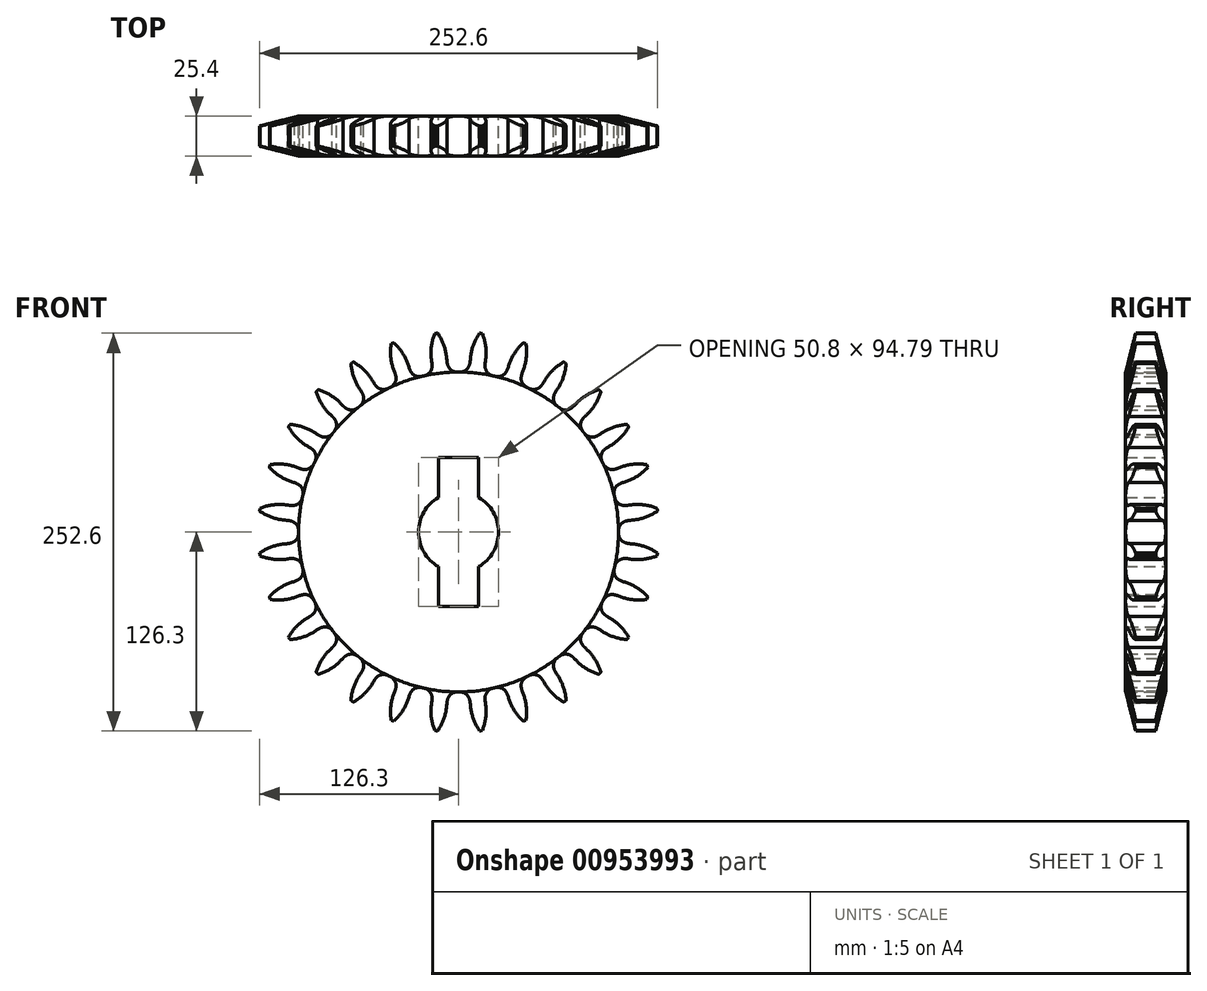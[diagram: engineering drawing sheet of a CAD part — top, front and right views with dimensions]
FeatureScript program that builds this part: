
annotation { "Feature Type Name" : "Feature", "Feature Type Description" : "" }
export const myFeature = defineFeature(function(context is Context, id is Id, definition is map)
    precondition{}
    {
        {
            var Q0;
            Q0=qCreatedBy(makeId("Front.planeOp"),FACE);
            var sketch = newSketch(context, id + "F0", { "sketchPlane" : qUnion([Q0])});
            skCircle(sketch, "E0", {"center": v(0, 0) * mm, "radius": 127 * mm});
            skLineSegment(sketch, "E1", {"start": v(0, 0) * mm, "end": v(0, 164.21) * mm, "construction": true});
            skLineSegment(sketch, "E2", {"start": v(0, 0) * mm, "end": v(174.47, 0) * mm, "construction": true});
            skCircle(sketch, "E3", {"center": v(0, 0) * mm, "radius": 25.4 * mm});
            skLineSegment(sketch, "E4.bottom", {"start": v(12.7, 47.4) * mm, "end": v(-12.7, 47.4) * mm});
            skLineSegment(sketch, "E4.top", {"start": v(12.7, -47.4) * mm, "end": v(-12.7, -47.4) * mm});
            skLineSegment(sketch, "E4.left", {"start": v(12.7, 47.4) * mm, "end": v(12.7, 22) * mm});
            skLineSegment(sketch, "E4.right", {"start": v(-12.7, 47.4) * mm, "end": v(-12.7, 22) * mm});
            skLineSegment(sketch, "E5.trimOffspring", {"start": v(-12.7, -22) * mm, "end": v(-12.7, -47.4) * mm});
            skLineSegment(sketch, "E6.trimOffspring", {"start": v(12.7, -22) * mm, "end": v(12.7, -47.4) * mm});
            skSolve(sketch);
        }
        {
            var Q0;
            Q0=makeQuery(id+"F0.imprint","IMPRINT",FACE,{"disambiguationData":[TD([[makeQuery(id+"F0.imprint","IMPRINT",EDGE,{"derivedFrom":sQuery(id+"F0.wireOp",EDGE,"E0")}),1.0]])]});
            extrude(context, id + "F1", {"entities" : qUnion([Q0]), "depth" : 25.4 * mm, "offsetDistance" : 25.4 * mm});
        }
        {
            var Q0;
            Q0=makeQuery(id+"F1.opExtrude","CAP_EDGE",EDGE,{"disambiguationData":[OSD([sQuery(id+"F0.wireOp",EDGE,"E0")])],"isStart":false});
            var Q1;
            Q1=makeQuery(id+"F1.opExtrude","CAP_EDGE",EDGE,{"disambiguationData":[OSD([sQuery(id+"F0.wireOp",EDGE,"E0")])],"isStart":true});
            chamfer(context, id + "F2", {"entities" : qUnion([Q0, Q1]), "chamferType" : ChamferType.TWO_OFFSETS, "width1" : 25.4 * mm, "oppositeDirection" : false, "width2" : 6.35 * mm, "tangentPropagation" : true});
        }
        {
            var Q0;
            Q0=makeQuery(id+"F0.imprint","IMPRINT",FACE,{"disambiguationData":[TD([[makeQuery(id+"F0.imprint","IMPRINT",EDGE,{"derivedFrom":sQuery(id+"F0.wireOp",EDGE,"E0")}),1.0]])]});
            var sketch = newSketch(context, id + "F3", { "sketchPlane" : qUnion([Q0])});
            skArc(sketch, "E7", {"start": v(0.8, 101.6) * mm, "mid": v(0, 101.6) * mm, "end": v(-0.8, 101.6) * mm});
            skLineSegment(sketch, "E8", {"start": v(-7.41, 108.46) * mm, "end": v(-7.1, 106.78) * mm});
            skLineSegment(sketch, "E9.MirrorCS", {"start": v(7.41, 108.46) * mm, "end": v(7.1, 106.78) * mm});
            skPoint(sketch, "E10.endSnap0", {"position": v(0, 101.6) * mm});
            skPoint(sketch, "E11.visualSharp", {"position": v(-6.1, 101.42) * mm});
            skArc(sketch, "E11.filletArc", {"start": v(-7.1, 106.78) * mm, "mid": v(-4.9, 103.04) * mm, "end": v(-0.8, 101.6) * mm});
            skPoint(sketch, "E12.visualSharp", {"position": v(6.1, 101.42) * mm});
            skArc(sketch, "E12.filletArc", {"start": v(0.8, 101.6) * mm, "mid": v(4.9, 103.04) * mm, "end": v(7.1, 106.78) * mm});
            skArc(sketch, "E13", {"start": v(22.64, 135.32) * mm, "mid": v(11.73, 123.75) * mm, "end": v(7.41, 108.46) * mm});
            skArc(sketch, "E14.MirrorCS", {"start": v(-22.64, 135.32) * mm, "mid": v(-11.73, 123.75) * mm, "end": v(-7.41, 108.46) * mm});
            skArc(sketch, "E15.1.0", {"start": v(-8.04, 136.96) * mm, "mid": v(-16.1, 123.26) * mm, "end": v(-16.9, 107.39) * mm});
            skArc(sketch, "E15.1.1", {"start": v(-52.18, 126.89) * mm, "mid": v(-38.98, 118.04) * mm, "end": v(-31.36, 104.09) * mm});
            skPoint(sketch, "E15.1.2", {"position": v(-16.63, 100.23) * mm});
            skPoint(sketch, "E15.1.3", {"position": v(-28.5, 97.52) * mm});
            skPoint(sketch, "E15.1.4", {"position": v(-22.6, 99.05) * mm});
            skArc(sketch, "E15.1.5", {"start": v(-30.68, 102.52) * mm, "mid": v(-27.7, 99.37) * mm, "end": v(-23.4, 98.87) * mm});
            skLineSegment(sketch, "E15.1.6", {"start": v(-31.36, 104.09) * mm, "end": v(-30.68, 102.52) * mm});
            skArc(sketch, "E15.1.7", {"start": v(-21.82, 99.23) * mm, "mid": v(-18.16, 101.55) * mm, "end": v(-16.84, 105.68) * mm});
            skLineSegment(sketch, "E15.1.8", {"start": v(-16.9, 107.39) * mm, "end": v(-16.84, 105.68) * mm});
            skArc(sketch, "E15.1.9", {"start": v(-21.82, 99.23) * mm, "mid": v(-22.6, 99.05) * mm, "end": v(-23.4, 98.87) * mm});
            skArc(sketch, "E15.2.0", {"start": v(-38.32, 131.74) * mm, "mid": v(-43.12, 116.59) * mm, "end": v(-40.38, 100.93) * mm});
            skArc(sketch, "E15.2.1", {"start": v(-79.1, 112.1) * mm, "mid": v(-64.27, 106.4) * mm, "end": v(-53.74, 94.5) * mm});
            skPoint(sketch, "E15.2.2", {"position": v(-38.51, 94.02) * mm});
            skPoint(sketch, "E15.2.3", {"position": v(-49.5, 88.73) * mm});
            skPoint(sketch, "E15.2.4", {"position": v(-44.08, 91.54) * mm});
            skArc(sketch, "E15.2.5", {"start": v(-52.72, 93.12) * mm, "mid": v(-49.12, 90.72) * mm, "end": v(-44.8, 91.19) * mm});
            skLineSegment(sketch, "E15.2.6", {"start": v(-53.74, 94.5) * mm, "end": v(-52.72, 93.12) * mm});
            skArc(sketch, "E15.2.7", {"start": v(-43.35, 91.89) * mm, "mid": v(-40.3, 94.96) * mm, "end": v(-39.93, 99.28) * mm});
            skLineSegment(sketch, "E15.2.8", {"start": v(-40.38, 100.93) * mm, "end": v(-39.93, 99.28) * mm});
            skArc(sketch, "E15.2.9", {"start": v(-43.35, 91.89) * mm, "mid": v(-44.08, 91.54) * mm, "end": v(-44.8, 91.19) * mm});
            skArc(sketch, "E15.3.0", {"start": v(-66.67, 119.91) * mm, "mid": v(-67.98, 104.07) * mm, "end": v(-61.83, 89.42) * mm});
            skArc(sketch, "E15.3.1", {"start": v(-102.07, 91.68) * mm, "mid": v(-86.33, 89.44) * mm, "end": v(-73.42, 80.17) * mm});
            skPoint(sketch, "E15.3.2", {"position": v(-58.47, 83.1) * mm});
            skPoint(sketch, "E15.3.3", {"position": v(-68, 75.5) * mm});
            skPoint(sketch, "E15.3.4", {"position": v(-63.35, 79.43) * mm});
            skArc(sketch, "E15.3.5", {"start": v(-72.12, 79.05) * mm, "mid": v(-68.07, 77.51) * mm, "end": v(-63.98, 78.93) * mm});
            skLineSegment(sketch, "E15.3.6", {"start": v(-73.42, 80.17) * mm, "end": v(-72.12, 79.05) * mm});
            skArc(sketch, "E15.3.7", {"start": v(-62.71, 79.93) * mm, "mid": v(-60.42, 83.61) * mm, "end": v(-61.02, 87.9) * mm});
            skLineSegment(sketch, "E15.3.8", {"start": v(-61.83, 89.42) * mm, "end": v(-61.02, 87.9) * mm});
            skArc(sketch, "E15.3.9", {"start": v(-62.71, 79.93) * mm, "mid": v(-63.35, 79.43) * mm, "end": v(-63.98, 78.93) * mm});
            skArc(sketch, "E15.4.0", {"start": v(-91.68, 102.07) * mm, "mid": v(-89.44, 86.33) * mm, "end": v(-80.17, 73.42) * mm});
            skArc(sketch, "E15.4.1", {"start": v(-119.91, 66.67) * mm, "mid": v(-104.07, 67.98) * mm, "end": v(-89.42, 61.83) * mm});
            skPoint(sketch, "E15.4.2", {"position": v(-75.5, 68) * mm});
            skPoint(sketch, "E15.4.3", {"position": v(-83.1, 58.47) * mm});
            skPoint(sketch, "E15.4.4", {"position": v(-79.43, 63.35) * mm});
            skArc(sketch, "E15.4.5", {"start": v(-87.9, 61.02) * mm, "mid": v(-83.61, 60.42) * mm, "end": v(-79.93, 62.71) * mm});
            skLineSegment(sketch, "E15.4.6", {"start": v(-89.42, 61.83) * mm, "end": v(-87.9, 61.02) * mm});
            skArc(sketch, "E15.4.7", {"start": v(-78.93, 63.98) * mm, "mid": v(-77.51, 68.07) * mm, "end": v(-79.05, 72.12) * mm});
            skLineSegment(sketch, "E15.4.8", {"start": v(-80.17, 73.42) * mm, "end": v(-79.05, 72.12) * mm});
            skArc(sketch, "E15.4.9", {"start": v(-78.93, 63.98) * mm, "mid": v(-79.43, 63.35) * mm, "end": v(-79.93, 62.71) * mm});
            skArc(sketch, "E15.5.0", {"start": v(-112.1, 79.1) * mm, "mid": v(-106.4, 64.27) * mm, "end": v(-94.5, 53.74) * mm});
            skArc(sketch, "E15.5.1", {"start": v(-131.74, 38.32) * mm, "mid": v(-116.59, 43.12) * mm, "end": v(-100.93, 40.38) * mm});
            skPoint(sketch, "E15.5.2", {"position": v(-88.73, 49.5) * mm});
            skPoint(sketch, "E15.5.3", {"position": v(-94.02, 38.51) * mm});
            skPoint(sketch, "E15.5.4", {"position": v(-91.54, 44.08) * mm});
            skArc(sketch, "E15.5.5", {"start": v(-99.28, 39.93) * mm, "mid": v(-94.96, 40.3) * mm, "end": v(-91.89, 43.35) * mm});
            skLineSegment(sketch, "E15.5.6", {"start": v(-100.93, 40.38) * mm, "end": v(-99.28, 39.93) * mm});
            skArc(sketch, "E15.5.7", {"start": v(-91.19, 44.8) * mm, "mid": v(-90.72, 49.12) * mm, "end": v(-93.12, 52.72) * mm});
            skLineSegment(sketch, "E15.5.8", {"start": v(-94.5, 53.74) * mm, "end": v(-93.12, 52.72) * mm});
            skArc(sketch, "E15.5.9", {"start": v(-91.19, 44.8) * mm, "mid": v(-91.54, 44.08) * mm, "end": v(-91.89, 43.35) * mm});
            skArc(sketch, "E15.6.0", {"start": v(-126.89, 52.18) * mm, "mid": v(-118.04, 38.98) * mm, "end": v(-104.09, 31.36) * mm});
            skArc(sketch, "E15.6.1", {"start": v(-136.96, 8.04) * mm, "mid": v(-123.26, 16.1) * mm, "end": v(-107.39, 16.9) * mm});
            skPoint(sketch, "E15.6.2", {"position": v(-97.52, 28.5) * mm});
            skPoint(sketch, "E15.6.3", {"position": v(-100.23, 16.63) * mm});
            skPoint(sketch, "E15.6.4", {"position": v(-99.05, 22.6) * mm});
            skArc(sketch, "E15.6.5", {"start": v(-105.68, 16.84) * mm, "mid": v(-101.55, 18.16) * mm, "end": v(-99.23, 21.82) * mm});
            skLineSegment(sketch, "E15.6.6", {"start": v(-107.39, 16.9) * mm, "end": v(-105.68, 16.84) * mm});
            skArc(sketch, "E15.6.7", {"start": v(-98.87, 23.4) * mm, "mid": v(-99.37, 27.7) * mm, "end": v(-102.52, 30.68) * mm});
            skLineSegment(sketch, "E15.6.8", {"start": v(-104.09, 31.36) * mm, "end": v(-102.52, 30.68) * mm});
            skArc(sketch, "E15.6.9", {"start": v(-98.87, 23.4) * mm, "mid": v(-99.05, 22.6) * mm, "end": v(-99.23, 21.82) * mm});
            skArc(sketch, "E15.7.0", {"start": v(-135.32, 22.64) * mm, "mid": v(-123.75, 11.73) * mm, "end": v(-108.46, 7.41) * mm});
            skArc(sketch, "E15.7.1", {"start": v(-135.32, -22.64) * mm, "mid": v(-123.75, -11.73) * mm, "end": v(-108.46, -7.41) * mm});
            skPoint(sketch, "E15.7.2", {"position": v(-101.42, 6.1) * mm});
            skPoint(sketch, "E15.7.3", {"position": v(-101.42, -6.1) * mm});
            skPoint(sketch, "E15.7.4", {"position": v(-101.6, 0) * mm});
            skArc(sketch, "E15.7.5", {"start": v(-106.78, -7.1) * mm, "mid": v(-103.04, -4.9) * mm, "end": v(-101.6, -0.8) * mm});
            skLineSegment(sketch, "E15.7.6", {"start": v(-108.46, -7.41) * mm, "end": v(-106.78, -7.1) * mm});
            skArc(sketch, "E15.7.7", {"start": v(-101.6, 0.8) * mm, "mid": v(-103.04, 4.9) * mm, "end": v(-106.78, 7.1) * mm});
            skLineSegment(sketch, "E15.7.8", {"start": v(-108.46, 7.41) * mm, "end": v(-106.78, 7.1) * mm});
            skArc(sketch, "E15.7.9", {"start": v(-101.6, 0.8) * mm, "mid": v(-101.6, 0) * mm, "end": v(-101.6, -0.8) * mm});
            skArc(sketch, "E15.8.0", {"start": v(-136.96, -8.04) * mm, "mid": v(-123.26, -16.1) * mm, "end": v(-107.39, -16.9) * mm});
            skArc(sketch, "E15.8.1", {"start": v(-126.89, -52.18) * mm, "mid": v(-118.04, -38.98) * mm, "end": v(-104.09, -31.36) * mm});
            skPoint(sketch, "E15.8.2", {"position": v(-100.23, -16.63) * mm});
            skPoint(sketch, "E15.8.3", {"position": v(-97.52, -28.5) * mm});
            skPoint(sketch, "E15.8.4", {"position": v(-99.05, -22.6) * mm});
            skArc(sketch, "E15.8.5", {"start": v(-102.52, -30.68) * mm, "mid": v(-99.37, -27.7) * mm, "end": v(-98.87, -23.4) * mm});
            skLineSegment(sketch, "E15.8.6", {"start": v(-104.09, -31.36) * mm, "end": v(-102.52, -30.68) * mm});
            skArc(sketch, "E15.8.7", {"start": v(-99.23, -21.82) * mm, "mid": v(-101.55, -18.16) * mm, "end": v(-105.68, -16.84) * mm});
            skLineSegment(sketch, "E15.8.8", {"start": v(-107.39, -16.9) * mm, "end": v(-105.68, -16.84) * mm});
            skArc(sketch, "E15.8.9", {"start": v(-99.23, -21.82) * mm, "mid": v(-99.05, -22.6) * mm, "end": v(-98.87, -23.4) * mm});
            skArc(sketch, "E15.9.0", {"start": v(-131.74, -38.32) * mm, "mid": v(-116.59, -43.12) * mm, "end": v(-100.93, -40.38) * mm});
            skArc(sketch, "E15.9.1", {"start": v(-112.1, -79.1) * mm, "mid": v(-106.4, -64.27) * mm, "end": v(-94.5, -53.74) * mm});
            skPoint(sketch, "E15.9.2", {"position": v(-94.02, -38.51) * mm});
            skPoint(sketch, "E15.9.3", {"position": v(-88.73, -49.5) * mm});
            skPoint(sketch, "E15.9.4", {"position": v(-91.54, -44.08) * mm});
            skArc(sketch, "E15.9.5", {"start": v(-93.12, -52.72) * mm, "mid": v(-90.72, -49.12) * mm, "end": v(-91.19, -44.8) * mm});
            skLineSegment(sketch, "E15.9.6", {"start": v(-94.5, -53.74) * mm, "end": v(-93.12, -52.72) * mm});
            skArc(sketch, "E15.9.7", {"start": v(-91.89, -43.35) * mm, "mid": v(-94.96, -40.3) * mm, "end": v(-99.28, -39.93) * mm});
            skLineSegment(sketch, "E15.9.8", {"start": v(-100.93, -40.38) * mm, "end": v(-99.28, -39.93) * mm});
            skArc(sketch, "E15.9.9", {"start": v(-91.89, -43.35) * mm, "mid": v(-91.54, -44.08) * mm, "end": v(-91.19, -44.8) * mm});
            skArc(sketch, "E15.10.0", {"start": v(-119.91, -66.67) * mm, "mid": v(-104.07, -67.98) * mm, "end": v(-89.42, -61.83) * mm});
            skArc(sketch, "E15.10.1", {"start": v(-91.68, -102.07) * mm, "mid": v(-89.44, -86.33) * mm, "end": v(-80.17, -73.42) * mm});
            skPoint(sketch, "E15.10.2", {"position": v(-83.1, -58.47) * mm});
            skPoint(sketch, "E15.10.3", {"position": v(-75.5, -68) * mm});
            skPoint(sketch, "E15.10.4", {"position": v(-79.43, -63.35) * mm});
            skArc(sketch, "E15.10.5", {"start": v(-79.05, -72.12) * mm, "mid": v(-77.51, -68.07) * mm, "end": v(-78.93, -63.98) * mm});
            skLineSegment(sketch, "E15.10.6", {"start": v(-80.17, -73.42) * mm, "end": v(-79.05, -72.12) * mm});
            skArc(sketch, "E15.10.7", {"start": v(-79.93, -62.71) * mm, "mid": v(-83.61, -60.42) * mm, "end": v(-87.9, -61.02) * mm});
            skLineSegment(sketch, "E15.10.8", {"start": v(-89.42, -61.83) * mm, "end": v(-87.9, -61.02) * mm});
            skArc(sketch, "E15.10.9", {"start": v(-79.93, -62.71) * mm, "mid": v(-79.43, -63.35) * mm, "end": v(-78.93, -63.98) * mm});
            skArc(sketch, "E15.11.0", {"start": v(-102.07, -91.68) * mm, "mid": v(-86.33, -89.44) * mm, "end": v(-73.42, -80.17) * mm});
            skArc(sketch, "E15.11.1", {"start": v(-66.67, -119.91) * mm, "mid": v(-67.98, -104.07) * mm, "end": v(-61.83, -89.42) * mm});
            skPoint(sketch, "E15.11.2", {"position": v(-68, -75.5) * mm});
            skPoint(sketch, "E15.11.3", {"position": v(-58.47, -83.1) * mm});
            skPoint(sketch, "E15.11.4", {"position": v(-63.35, -79.43) * mm});
            skArc(sketch, "E15.11.5", {"start": v(-61.02, -87.9) * mm, "mid": v(-60.42, -83.61) * mm, "end": v(-62.71, -79.93) * mm});
            skLineSegment(sketch, "E15.11.6", {"start": v(-61.83, -89.42) * mm, "end": v(-61.02, -87.9) * mm});
            skArc(sketch, "E15.11.7", {"start": v(-63.98, -78.93) * mm, "mid": v(-68.07, -77.51) * mm, "end": v(-72.12, -79.05) * mm});
            skLineSegment(sketch, "E15.11.8", {"start": v(-73.42, -80.17) * mm, "end": v(-72.12, -79.05) * mm});
            skArc(sketch, "E15.11.9", {"start": v(-63.98, -78.93) * mm, "mid": v(-63.35, -79.43) * mm, "end": v(-62.71, -79.93) * mm});
            skArc(sketch, "E15.12.0", {"start": v(-79.1, -112.1) * mm, "mid": v(-64.27, -106.4) * mm, "end": v(-53.74, -94.5) * mm});
            skArc(sketch, "E15.12.1", {"start": v(-38.32, -131.74) * mm, "mid": v(-43.12, -116.59) * mm, "end": v(-40.38, -100.93) * mm});
            skPoint(sketch, "E15.12.2", {"position": v(-49.5, -88.73) * mm});
            skPoint(sketch, "E15.12.3", {"position": v(-38.51, -94.02) * mm});
            skPoint(sketch, "E15.12.4", {"position": v(-44.08, -91.54) * mm});
            skArc(sketch, "E15.12.5", {"start": v(-39.93, -99.28) * mm, "mid": v(-40.3, -94.96) * mm, "end": v(-43.35, -91.89) * mm});
            skLineSegment(sketch, "E15.12.6", {"start": v(-40.38, -100.93) * mm, "end": v(-39.93, -99.28) * mm});
            skArc(sketch, "E15.12.7", {"start": v(-44.8, -91.19) * mm, "mid": v(-49.12, -90.72) * mm, "end": v(-52.72, -93.12) * mm});
            skLineSegment(sketch, "E15.12.8", {"start": v(-53.74, -94.5) * mm, "end": v(-52.72, -93.12) * mm});
            skArc(sketch, "E15.12.9", {"start": v(-44.8, -91.19) * mm, "mid": v(-44.08, -91.54) * mm, "end": v(-43.35, -91.89) * mm});
            skArc(sketch, "E15.13.0", {"start": v(-52.18, -126.89) * mm, "mid": v(-38.98, -118.04) * mm, "end": v(-31.36, -104.09) * mm});
            skArc(sketch, "E15.13.1", {"start": v(-8.04, -136.96) * mm, "mid": v(-16.1, -123.26) * mm, "end": v(-16.9, -107.39) * mm});
            skPoint(sketch, "E15.13.2", {"position": v(-28.5, -97.52) * mm});
            skPoint(sketch, "E15.13.3", {"position": v(-16.63, -100.23) * mm});
            skPoint(sketch, "E15.13.4", {"position": v(-22.6, -99.05) * mm});
            skArc(sketch, "E15.13.5", {"start": v(-16.84, -105.68) * mm, "mid": v(-18.16, -101.55) * mm, "end": v(-21.82, -99.23) * mm});
            skLineSegment(sketch, "E15.13.6", {"start": v(-16.9, -107.39) * mm, "end": v(-16.84, -105.68) * mm});
            skArc(sketch, "E15.13.7", {"start": v(-23.4, -98.87) * mm, "mid": v(-27.7, -99.37) * mm, "end": v(-30.68, -102.52) * mm});
            skLineSegment(sketch, "E15.13.8", {"start": v(-31.36, -104.09) * mm, "end": v(-30.68, -102.52) * mm});
            skArc(sketch, "E15.13.9", {"start": v(-23.4, -98.87) * mm, "mid": v(-22.6, -99.05) * mm, "end": v(-21.82, -99.23) * mm});
            skArc(sketch, "E15.14.0", {"start": v(-22.64, -135.32) * mm, "mid": v(-11.73, -123.75) * mm, "end": v(-7.41, -108.46) * mm});
            skArc(sketch, "E15.14.1", {"start": v(22.64, -135.32) * mm, "mid": v(11.73, -123.75) * mm, "end": v(7.41, -108.46) * mm});
            skPoint(sketch, "E15.14.2", {"position": v(-6.1, -101.42) * mm});
            skPoint(sketch, "E15.14.3", {"position": v(6.1, -101.42) * mm});
            skPoint(sketch, "E15.14.4", {"position": v(0, -101.6) * mm});
            skArc(sketch, "E15.14.5", {"start": v(7.1, -106.78) * mm, "mid": v(4.9, -103.04) * mm, "end": v(0.8, -101.6) * mm});
            skLineSegment(sketch, "E15.14.6", {"start": v(7.41, -108.46) * mm, "end": v(7.1, -106.78) * mm});
            skArc(sketch, "E15.14.7", {"start": v(-0.8, -101.6) * mm, "mid": v(-4.9, -103.04) * mm, "end": v(-7.1, -106.78) * mm});
            skLineSegment(sketch, "E15.14.8", {"start": v(-7.41, -108.46) * mm, "end": v(-7.1, -106.78) * mm});
            skArc(sketch, "E15.14.9", {"start": v(-0.8, -101.6) * mm, "mid": v(0, -101.6) * mm, "end": v(0.8, -101.6) * mm});
            skArc(sketch, "E15.15.0", {"start": v(8.04, -136.96) * mm, "mid": v(16.1, -123.26) * mm, "end": v(16.9, -107.39) * mm});
            skArc(sketch, "E15.15.1", {"start": v(52.18, -126.89) * mm, "mid": v(38.98, -118.04) * mm, "end": v(31.36, -104.09) * mm});
            skPoint(sketch, "E15.15.2", {"position": v(16.63, -100.23) * mm});
            skPoint(sketch, "E15.15.3", {"position": v(28.5, -97.52) * mm});
            skPoint(sketch, "E15.15.4", {"position": v(22.6, -99.05) * mm});
            skArc(sketch, "E15.15.5", {"start": v(30.68, -102.52) * mm, "mid": v(27.7, -99.37) * mm, "end": v(23.4, -98.87) * mm});
            skLineSegment(sketch, "E15.15.6", {"start": v(31.36, -104.09) * mm, "end": v(30.68, -102.52) * mm});
            skArc(sketch, "E15.15.7", {"start": v(21.82, -99.23) * mm, "mid": v(18.16, -101.55) * mm, "end": v(16.84, -105.68) * mm});
            skLineSegment(sketch, "E15.15.8", {"start": v(16.9, -107.39) * mm, "end": v(16.84, -105.68) * mm});
            skArc(sketch, "E15.15.9", {"start": v(21.82, -99.23) * mm, "mid": v(22.6, -99.05) * mm, "end": v(23.4, -98.87) * mm});
            skArc(sketch, "E15.16.0", {"start": v(38.32, -131.74) * mm, "mid": v(43.12, -116.59) * mm, "end": v(40.38, -100.93) * mm});
            skArc(sketch, "E15.16.1", {"start": v(79.1, -112.1) * mm, "mid": v(64.27, -106.4) * mm, "end": v(53.74, -94.5) * mm});
            skPoint(sketch, "E15.16.2", {"position": v(38.51, -94.02) * mm});
            skPoint(sketch, "E15.16.3", {"position": v(49.5, -88.73) * mm});
            skPoint(sketch, "E15.16.4", {"position": v(44.08, -91.54) * mm});
            skArc(sketch, "E15.16.5", {"start": v(52.72, -93.12) * mm, "mid": v(49.12, -90.72) * mm, "end": v(44.8, -91.19) * mm});
            skLineSegment(sketch, "E15.16.6", {"start": v(53.74, -94.5) * mm, "end": v(52.72, -93.12) * mm});
            skArc(sketch, "E15.16.7", {"start": v(43.35, -91.89) * mm, "mid": v(40.3, -94.96) * mm, "end": v(39.93, -99.28) * mm});
            skLineSegment(sketch, "E15.16.8", {"start": v(40.38, -100.93) * mm, "end": v(39.93, -99.28) * mm});
            skArc(sketch, "E15.16.9", {"start": v(43.35, -91.89) * mm, "mid": v(44.08, -91.54) * mm, "end": v(44.8, -91.19) * mm});
            skArc(sketch, "E15.17.0", {"start": v(66.67, -119.91) * mm, "mid": v(67.98, -104.07) * mm, "end": v(61.83, -89.42) * mm});
            skArc(sketch, "E15.17.1", {"start": v(102.07, -91.68) * mm, "mid": v(86.33, -89.44) * mm, "end": v(73.42, -80.17) * mm});
            skPoint(sketch, "E15.17.2", {"position": v(58.47, -83.1) * mm});
            skPoint(sketch, "E15.17.3", {"position": v(68, -75.5) * mm});
            skPoint(sketch, "E15.17.4", {"position": v(63.35, -79.43) * mm});
            skArc(sketch, "E15.17.5", {"start": v(72.12, -79.05) * mm, "mid": v(68.07, -77.51) * mm, "end": v(63.98, -78.93) * mm});
            skLineSegment(sketch, "E15.17.6", {"start": v(73.42, -80.17) * mm, "end": v(72.12, -79.05) * mm});
            skArc(sketch, "E15.17.7", {"start": v(62.71, -79.93) * mm, "mid": v(60.42, -83.61) * mm, "end": v(61.02, -87.9) * mm});
            skLineSegment(sketch, "E15.17.8", {"start": v(61.83, -89.42) * mm, "end": v(61.02, -87.9) * mm});
            skArc(sketch, "E15.17.9", {"start": v(62.71, -79.93) * mm, "mid": v(63.35, -79.43) * mm, "end": v(63.98, -78.93) * mm});
            skArc(sketch, "E15.18.0", {"start": v(91.68, -102.07) * mm, "mid": v(89.44, -86.33) * mm, "end": v(80.17, -73.42) * mm});
            skArc(sketch, "E15.18.1", {"start": v(119.91, -66.67) * mm, "mid": v(104.07, -67.98) * mm, "end": v(89.42, -61.83) * mm});
            skPoint(sketch, "E15.18.2", {"position": v(75.5, -68) * mm});
            skPoint(sketch, "E15.18.3", {"position": v(83.1, -58.47) * mm});
            skPoint(sketch, "E15.18.4", {"position": v(79.43, -63.35) * mm});
            skArc(sketch, "E15.18.5", {"start": v(87.9, -61.02) * mm, "mid": v(83.61, -60.42) * mm, "end": v(79.93, -62.71) * mm});
            skLineSegment(sketch, "E15.18.6", {"start": v(89.42, -61.83) * mm, "end": v(87.9, -61.02) * mm});
            skArc(sketch, "E15.18.7", {"start": v(78.93, -63.98) * mm, "mid": v(77.51, -68.07) * mm, "end": v(79.05, -72.12) * mm});
            skLineSegment(sketch, "E15.18.8", {"start": v(80.17, -73.42) * mm, "end": v(79.05, -72.12) * mm});
            skArc(sketch, "E15.18.9", {"start": v(78.93, -63.98) * mm, "mid": v(79.43, -63.35) * mm, "end": v(79.93, -62.71) * mm});
            skArc(sketch, "E15.19.0", {"start": v(112.1, -79.1) * mm, "mid": v(106.4, -64.27) * mm, "end": v(94.5, -53.74) * mm});
            skArc(sketch, "E15.19.1", {"start": v(131.74, -38.32) * mm, "mid": v(116.59, -43.12) * mm, "end": v(100.93, -40.38) * mm});
            skPoint(sketch, "E15.19.2", {"position": v(88.73, -49.5) * mm});
            skPoint(sketch, "E15.19.3", {"position": v(94.02, -38.51) * mm});
            skPoint(sketch, "E15.19.4", {"position": v(91.54, -44.08) * mm});
            skArc(sketch, "E15.19.5", {"start": v(99.28, -39.93) * mm, "mid": v(94.96, -40.3) * mm, "end": v(91.89, -43.35) * mm});
            skLineSegment(sketch, "E15.19.6", {"start": v(100.93, -40.38) * mm, "end": v(99.28, -39.93) * mm});
            skArc(sketch, "E15.19.7", {"start": v(91.19, -44.8) * mm, "mid": v(90.72, -49.12) * mm, "end": v(93.12, -52.72) * mm});
            skLineSegment(sketch, "E15.19.8", {"start": v(94.5, -53.74) * mm, "end": v(93.12, -52.72) * mm});
            skArc(sketch, "E15.19.9", {"start": v(91.19, -44.8) * mm, "mid": v(91.54, -44.08) * mm, "end": v(91.89, -43.35) * mm});
            skArc(sketch, "E15.20.0", {"start": v(126.89, -52.18) * mm, "mid": v(118.04, -38.98) * mm, "end": v(104.09, -31.36) * mm});
            skArc(sketch, "E15.20.1", {"start": v(136.96, -8.04) * mm, "mid": v(123.26, -16.1) * mm, "end": v(107.39, -16.9) * mm});
            skPoint(sketch, "E15.20.2", {"position": v(97.52, -28.5) * mm});
            skPoint(sketch, "E15.20.3", {"position": v(100.23, -16.63) * mm});
            skPoint(sketch, "E15.20.4", {"position": v(99.05, -22.6) * mm});
            skArc(sketch, "E15.20.5", {"start": v(105.68, -16.84) * mm, "mid": v(101.55, -18.16) * mm, "end": v(99.23, -21.82) * mm});
            skLineSegment(sketch, "E15.20.6", {"start": v(107.39, -16.9) * mm, "end": v(105.68, -16.84) * mm});
            skArc(sketch, "E15.20.7", {"start": v(98.87, -23.4) * mm, "mid": v(99.37, -27.7) * mm, "end": v(102.52, -30.68) * mm});
            skLineSegment(sketch, "E15.20.8", {"start": v(104.09, -31.36) * mm, "end": v(102.52, -30.68) * mm});
            skArc(sketch, "E15.20.9", {"start": v(98.87, -23.4) * mm, "mid": v(99.05, -22.6) * mm, "end": v(99.23, -21.82) * mm});
            skArc(sketch, "E15.21.0", {"start": v(135.32, -22.64) * mm, "mid": v(123.75, -11.73) * mm, "end": v(108.46, -7.41) * mm});
            skArc(sketch, "E15.21.1", {"start": v(135.32, 22.64) * mm, "mid": v(123.75, 11.73) * mm, "end": v(108.46, 7.41) * mm});
            skPoint(sketch, "E15.21.2", {"position": v(101.42, -6.1) * mm});
            skPoint(sketch, "E15.21.3", {"position": v(101.42, 6.1) * mm});
            skPoint(sketch, "E15.21.4", {"position": v(101.6, 0) * mm});
            skArc(sketch, "E15.21.5", {"start": v(106.78, 7.1) * mm, "mid": v(103.04, 4.9) * mm, "end": v(101.6, 0.8) * mm});
            skLineSegment(sketch, "E15.21.6", {"start": v(108.46, 7.41) * mm, "end": v(106.78, 7.1) * mm});
            skArc(sketch, "E15.21.7", {"start": v(101.6, -0.8) * mm, "mid": v(103.04, -4.9) * mm, "end": v(106.78, -7.1) * mm});
            skLineSegment(sketch, "E15.21.8", {"start": v(108.46, -7.41) * mm, "end": v(106.78, -7.1) * mm});
            skArc(sketch, "E15.21.9", {"start": v(101.6, -0.8) * mm, "mid": v(101.6, 0) * mm, "end": v(101.6, 0.8) * mm});
            skArc(sketch, "E15.22.0", {"start": v(136.96, 8.04) * mm, "mid": v(123.26, 16.1) * mm, "end": v(107.39, 16.9) * mm});
            skArc(sketch, "E15.22.1", {"start": v(126.89, 52.18) * mm, "mid": v(118.04, 38.98) * mm, "end": v(104.09, 31.36) * mm});
            skPoint(sketch, "E15.22.2", {"position": v(100.23, 16.63) * mm});
            skPoint(sketch, "E15.22.3", {"position": v(97.52, 28.5) * mm});
            skPoint(sketch, "E15.22.4", {"position": v(99.05, 22.6) * mm});
            skArc(sketch, "E15.22.5", {"start": v(102.52, 30.68) * mm, "mid": v(99.37, 27.7) * mm, "end": v(98.87, 23.4) * mm});
            skLineSegment(sketch, "E15.22.6", {"start": v(104.09, 31.36) * mm, "end": v(102.52, 30.68) * mm});
            skArc(sketch, "E15.22.7", {"start": v(99.23, 21.82) * mm, "mid": v(101.55, 18.16) * mm, "end": v(105.68, 16.84) * mm});
            skLineSegment(sketch, "E15.22.8", {"start": v(107.39, 16.9) * mm, "end": v(105.68, 16.84) * mm});
            skArc(sketch, "E15.22.9", {"start": v(99.23, 21.82) * mm, "mid": v(99.05, 22.6) * mm, "end": v(98.87, 23.4) * mm});
            skArc(sketch, "E15.23.0", {"start": v(131.74, 38.32) * mm, "mid": v(116.59, 43.12) * mm, "end": v(100.93, 40.38) * mm});
            skArc(sketch, "E15.23.1", {"start": v(112.1, 79.1) * mm, "mid": v(106.4, 64.27) * mm, "end": v(94.5, 53.74) * mm});
            skPoint(sketch, "E15.23.2", {"position": v(94.02, 38.51) * mm});
            skPoint(sketch, "E15.23.3", {"position": v(88.73, 49.5) * mm});
            skPoint(sketch, "E15.23.4", {"position": v(91.54, 44.08) * mm});
            skArc(sketch, "E15.23.5", {"start": v(93.12, 52.72) * mm, "mid": v(90.72, 49.12) * mm, "end": v(91.19, 44.8) * mm});
            skLineSegment(sketch, "E15.23.6", {"start": v(94.5, 53.74) * mm, "end": v(93.12, 52.72) * mm});
            skArc(sketch, "E15.23.7", {"start": v(91.89, 43.35) * mm, "mid": v(94.96, 40.3) * mm, "end": v(99.28, 39.93) * mm});
            skLineSegment(sketch, "E15.23.8", {"start": v(100.93, 40.38) * mm, "end": v(99.28, 39.93) * mm});
            skArc(sketch, "E15.23.9", {"start": v(91.89, 43.35) * mm, "mid": v(91.54, 44.08) * mm, "end": v(91.19, 44.8) * mm});
            skArc(sketch, "E15.24.0", {"start": v(119.91, 66.67) * mm, "mid": v(104.07, 67.98) * mm, "end": v(89.42, 61.83) * mm});
            skArc(sketch, "E15.24.1", {"start": v(91.68, 102.07) * mm, "mid": v(89.44, 86.33) * mm, "end": v(80.17, 73.42) * mm});
            skPoint(sketch, "E15.24.2", {"position": v(83.1, 58.47) * mm});
            skPoint(sketch, "E15.24.3", {"position": v(75.5, 68) * mm});
            skPoint(sketch, "E15.24.4", {"position": v(79.43, 63.35) * mm});
            skArc(sketch, "E15.24.5", {"start": v(79.05, 72.12) * mm, "mid": v(77.51, 68.07) * mm, "end": v(78.93, 63.98) * mm});
            skLineSegment(sketch, "E15.24.6", {"start": v(80.17, 73.42) * mm, "end": v(79.05, 72.12) * mm});
            skArc(sketch, "E15.24.7", {"start": v(79.93, 62.71) * mm, "mid": v(83.61, 60.42) * mm, "end": v(87.9, 61.02) * mm});
            skLineSegment(sketch, "E15.24.8", {"start": v(89.42, 61.83) * mm, "end": v(87.9, 61.02) * mm});
            skArc(sketch, "E15.24.9", {"start": v(79.93, 62.71) * mm, "mid": v(79.43, 63.35) * mm, "end": v(78.93, 63.98) * mm});
            skArc(sketch, "E15.25.0", {"start": v(102.07, 91.68) * mm, "mid": v(86.33, 89.44) * mm, "end": v(73.42, 80.17) * mm});
            skArc(sketch, "E15.25.1", {"start": v(66.67, 119.91) * mm, "mid": v(67.98, 104.07) * mm, "end": v(61.83, 89.42) * mm});
            skPoint(sketch, "E15.25.2", {"position": v(68, 75.5) * mm});
            skPoint(sketch, "E15.25.3", {"position": v(58.47, 83.1) * mm});
            skPoint(sketch, "E15.25.4", {"position": v(63.35, 79.43) * mm});
            skArc(sketch, "E15.25.5", {"start": v(61.02, 87.9) * mm, "mid": v(60.42, 83.61) * mm, "end": v(62.71, 79.93) * mm});
            skLineSegment(sketch, "E15.25.6", {"start": v(61.83, 89.42) * mm, "end": v(61.02, 87.9) * mm});
            skArc(sketch, "E15.25.7", {"start": v(63.98, 78.93) * mm, "mid": v(68.07, 77.51) * mm, "end": v(72.12, 79.05) * mm});
            skLineSegment(sketch, "E15.25.8", {"start": v(73.42, 80.17) * mm, "end": v(72.12, 79.05) * mm});
            skArc(sketch, "E15.25.9", {"start": v(63.98, 78.93) * mm, "mid": v(63.35, 79.43) * mm, "end": v(62.71, 79.93) * mm});
            skArc(sketch, "E15.26.0", {"start": v(79.1, 112.1) * mm, "mid": v(64.27, 106.4) * mm, "end": v(53.74, 94.5) * mm});
            skArc(sketch, "E15.26.1", {"start": v(38.32, 131.74) * mm, "mid": v(43.12, 116.59) * mm, "end": v(40.38, 100.93) * mm});
            skPoint(sketch, "E15.26.2", {"position": v(49.5, 88.73) * mm});
            skPoint(sketch, "E15.26.3", {"position": v(38.51, 94.02) * mm});
            skPoint(sketch, "E15.26.4", {"position": v(44.08, 91.54) * mm});
            skArc(sketch, "E15.26.5", {"start": v(39.93, 99.28) * mm, "mid": v(40.3, 94.96) * mm, "end": v(43.35, 91.89) * mm});
            skLineSegment(sketch, "E15.26.6", {"start": v(40.38, 100.93) * mm, "end": v(39.93, 99.28) * mm});
            skArc(sketch, "E15.26.7", {"start": v(44.8, 91.19) * mm, "mid": v(49.12, 90.72) * mm, "end": v(52.72, 93.12) * mm});
            skLineSegment(sketch, "E15.26.8", {"start": v(53.74, 94.5) * mm, "end": v(52.72, 93.12) * mm});
            skArc(sketch, "E15.26.9", {"start": v(44.8, 91.19) * mm, "mid": v(44.08, 91.54) * mm, "end": v(43.35, 91.89) * mm});
            skArc(sketch, "E15.27.0", {"start": v(52.18, 126.89) * mm, "mid": v(38.98, 118.04) * mm, "end": v(31.36, 104.09) * mm});
            skArc(sketch, "E15.27.1", {"start": v(8.04, 136.96) * mm, "mid": v(16.1, 123.26) * mm, "end": v(16.9, 107.39) * mm});
            skPoint(sketch, "E15.27.2", {"position": v(28.5, 97.52) * mm});
            skPoint(sketch, "E15.27.3", {"position": v(16.63, 100.23) * mm});
            skPoint(sketch, "E15.27.4", {"position": v(22.6, 99.05) * mm});
            skArc(sketch, "E15.27.5", {"start": v(16.84, 105.68) * mm, "mid": v(18.16, 101.55) * mm, "end": v(21.82, 99.23) * mm});
            skLineSegment(sketch, "E15.27.6", {"start": v(16.9, 107.39) * mm, "end": v(16.84, 105.68) * mm});
            skArc(sketch, "E15.27.7", {"start": v(23.4, 98.87) * mm, "mid": v(27.7, 99.37) * mm, "end": v(30.68, 102.52) * mm});
            skLineSegment(sketch, "E15.27.8", {"start": v(31.36, 104.09) * mm, "end": v(30.68, 102.52) * mm});
            skArc(sketch, "E15.27.9", {"start": v(23.4, 98.87) * mm, "mid": v(22.6, 99.05) * mm, "end": v(21.82, 99.23) * mm});
            skSolve(sketch);
        }
        {
            var Q0;
            {var subQ0=sQuery(id+"F3.wireOp",EDGE,"2a13c689-51f3-40da-a152-91a346033ccf.7.0");Q0=makeQuery(id+"F3.imprint","IMPRINT",FACE,{"disambiguationData":[TD([[makeQuery(id+"F3.imprint","IMPRINT",EDGE,{"derivedFrom":subQ0}),1.0]])]});}
            var Q1;
            {var subQ0=sQuery(id+"F3.wireOp",EDGE,"2a13c689-51f3-40da-a152-91a346033ccf.4.0");Q1=makeQuery(id+"F3.imprint","IMPRINT",FACE,{"disambiguationData":[TD([[makeQuery(id+"F3.imprint","IMPRINT",EDGE,{"derivedFrom":subQ0}),1.0]])]});}
            var Q2;
            {var subQ0=sQuery(id+"F3.wireOp",EDGE,"2a13c689-51f3-40da-a152-91a346033ccf.2.0");Q2=makeQuery(id+"F3.imprint","IMPRINT",FACE,{"disambiguationData":[TD([[makeQuery(id+"F3.imprint","IMPRINT",EDGE,{"derivedFrom":subQ0}),1.0]])]});}
            var Q3;
            {var subQ0=sQuery(id+"F3.wireOp",EDGE,"2a13c689-51f3-40da-a152-91a346033ccf.1.0");Q3=makeQuery(id+"F3.imprint","IMPRINT",FACE,{"disambiguationData":[TD([[makeQuery(id+"F3.imprint","IMPRINT",EDGE,{"derivedFrom":subQ0}),1.0]])]});}
            var Q4;
            Q4=makeQuery(id+"F3.imprint","IMPRINT",FACE,{"disambiguationData":[TD([[makeQuery(id+"F3.imprint","IMPRINT",EDGE,{"derivedFrom":sQuery(id+"F3.wireOp",EDGE,"E7")}),-1.0]])]});
            var Q5;
            {var subQ0=sQuery(id+"F3.wireOp",EDGE,"2d3145ba-c956-4d6d-ab4f-1630ba25d74d.2.27.0");Q5=makeQuery(id+"F3.imprint","IMPRINT",FACE,{"disambiguationData":[TD([[makeQuery(id+"F3.imprint","IMPRINT",EDGE,{"derivedFrom":subQ0}),1.0]])]});}
            var Q6;
            {var subQ0=sQuery(id+"F3.wireOp",EDGE,"2d3145ba-c956-4d6d-ab4f-1630ba25d74d.2.26.0");Q6=makeQuery(id+"F3.imprint","IMPRINT",FACE,{"disambiguationData":[TD([[makeQuery(id+"F3.imprint","IMPRINT",EDGE,{"derivedFrom":subQ0}),1.0]])]});}
            var Q7;
            {var subQ0=sQuery(id+"F3.wireOp",EDGE,"2d3145ba-c956-4d6d-ab4f-1630ba25d74d.2.25.0");Q7=makeQuery(id+"F3.imprint","IMPRINT",FACE,{"disambiguationData":[TD([[makeQuery(id+"F3.imprint","IMPRINT",EDGE,{"derivedFrom":subQ0}),1.0]])]});}
            var Q8;
            {var subQ0=sQuery(id+"F3.wireOp",EDGE,"2d3145ba-c956-4d6d-ab4f-1630ba25d74d.2.24.0");Q8=makeQuery(id+"F3.imprint","IMPRINT",FACE,{"disambiguationData":[TD([[makeQuery(id+"F3.imprint","IMPRINT",EDGE,{"derivedFrom":subQ0}),1.0]])]});}
            var Q9;
            {var subQ0=sQuery(id+"F3.wireOp",EDGE,"2a13c689-51f3-40da-a152-91a346033ccf.23.0");Q9=makeQuery(id+"F3.imprint","IMPRINT",FACE,{"disambiguationData":[TD([[makeQuery(id+"F3.imprint","IMPRINT",EDGE,{"derivedFrom":subQ0}),1.0]])]});}
            var Q10;
            {var subQ0=sQuery(id+"F3.wireOp",EDGE,"2a13c689-51f3-40da-a152-91a346033ccf.22.0");Q10=makeQuery(id+"F3.imprint","IMPRINT",FACE,{"disambiguationData":[TD([[makeQuery(id+"F3.imprint","IMPRINT",EDGE,{"derivedFrom":subQ0}),1.0]])]});}
            var Q11;
            {var subQ0=sQuery(id+"F3.wireOp",EDGE,"2a13c689-51f3-40da-a152-91a346033ccf.21.0");Q11=makeQuery(id+"F3.imprint","IMPRINT",FACE,{"disambiguationData":[TD([[makeQuery(id+"F3.imprint","IMPRINT",EDGE,{"derivedFrom":subQ0}),1.0]])]});}
            var Q12;
            {var subQ0=sQuery(id+"F3.wireOp",EDGE,"2a13c689-51f3-40da-a152-91a346033ccf.20.0");Q12=makeQuery(id+"F3.imprint","IMPRINT",FACE,{"disambiguationData":[TD([[makeQuery(id+"F3.imprint","IMPRINT",EDGE,{"derivedFrom":subQ0}),1.0]])]});}
            var Q13;
            {var subQ0=sQuery(id+"F3.wireOp",EDGE,"2a13c689-51f3-40da-a152-91a346033ccf.19.0");Q13=makeQuery(id+"F3.imprint","IMPRINT",FACE,{"disambiguationData":[TD([[makeQuery(id+"F3.imprint","IMPRINT",EDGE,{"derivedFrom":subQ0}),1.0]])]});}
            var Q14;
            {var subQ0=sQuery(id+"F3.wireOp",EDGE,"2a13c689-51f3-40da-a152-91a346033ccf.18.0");Q14=makeQuery(id+"F3.imprint","IMPRINT",FACE,{"disambiguationData":[TD([[makeQuery(id+"F3.imprint","IMPRINT",EDGE,{"derivedFrom":subQ0}),1.0]])]});}
            var Q15;
            {var subQ0=sQuery(id+"F3.wireOp",EDGE,"2a13c689-51f3-40da-a152-91a346033ccf.17.0");Q15=makeQuery(id+"F3.imprint","IMPRINT",FACE,{"disambiguationData":[TD([[makeQuery(id+"F3.imprint","IMPRINT",EDGE,{"derivedFrom":subQ0}),1.0]])]});}
            var Q16;
            {var subQ0=sQuery(id+"F3.wireOp",EDGE,"2a13c689-51f3-40da-a152-91a346033ccf.16.0");Q16=makeQuery(id+"F3.imprint","IMPRINT",FACE,{"disambiguationData":[TD([[makeQuery(id+"F3.imprint","IMPRINT",EDGE,{"derivedFrom":subQ0}),1.0]])]});}
            var Q17;
            {var subQ0=sQuery(id+"F3.wireOp",EDGE,"2a13c689-51f3-40da-a152-91a346033ccf.15.0");Q17=makeQuery(id+"F3.imprint","IMPRINT",FACE,{"disambiguationData":[TD([[makeQuery(id+"F3.imprint","IMPRINT",EDGE,{"derivedFrom":subQ0}),1.0]])]});}
            var Q18;
            {var subQ0=sQuery(id+"F3.wireOp",EDGE,"2a13c689-51f3-40da-a152-91a346033ccf.14.0");Q18=makeQuery(id+"F3.imprint","IMPRINT",FACE,{"disambiguationData":[TD([[makeQuery(id+"F3.imprint","IMPRINT",EDGE,{"derivedFrom":subQ0}),1.0]])]});}
            var Q19;
            {var subQ0=sQuery(id+"F3.wireOp",EDGE,"2a13c689-51f3-40da-a152-91a346033ccf.13.0");Q19=makeQuery(id+"F3.imprint","IMPRINT",FACE,{"disambiguationData":[TD([[makeQuery(id+"F3.imprint","IMPRINT",EDGE,{"derivedFrom":subQ0}),1.0]])]});}
            var Q20;
            {var subQ0=sQuery(id+"F3.wireOp",EDGE,"2a13c689-51f3-40da-a152-91a346033ccf.12.0");Q20=makeQuery(id+"F3.imprint","IMPRINT",FACE,{"disambiguationData":[TD([[makeQuery(id+"F3.imprint","IMPRINT",EDGE,{"derivedFrom":subQ0}),1.0]])]});}
            var Q21;
            {var subQ0=sQuery(id+"F3.wireOp",EDGE,"2a13c689-51f3-40da-a152-91a346033ccf.11.0");Q21=makeQuery(id+"F3.imprint","IMPRINT",FACE,{"disambiguationData":[TD([[makeQuery(id+"F3.imprint","IMPRINT",EDGE,{"derivedFrom":subQ0}),1.0]])]});}
            var Q22;
            {var subQ0=sQuery(id+"F3.wireOp",EDGE,"2a13c689-51f3-40da-a152-91a346033ccf.10.0");Q22=makeQuery(id+"F3.imprint","IMPRINT",FACE,{"disambiguationData":[TD([[makeQuery(id+"F3.imprint","IMPRINT",EDGE,{"derivedFrom":subQ0}),1.0]])]});}
            var Q23;
            {var subQ0=sQuery(id+"F3.wireOp",EDGE,"2a13c689-51f3-40da-a152-91a346033ccf.9.0");Q23=makeQuery(id+"F3.imprint","IMPRINT",FACE,{"disambiguationData":[TD([[makeQuery(id+"F3.imprint","IMPRINT",EDGE,{"derivedFrom":subQ0}),1.0]])]});}
            var Q24;
            {var subQ0=sQuery(id+"F3.wireOp",EDGE,"2a13c689-51f3-40da-a152-91a346033ccf.8.0");Q24=makeQuery(id+"F3.imprint","IMPRINT",FACE,{"disambiguationData":[TD([[makeQuery(id+"F3.imprint","IMPRINT",EDGE,{"derivedFrom":subQ0}),1.0]])]});}
            var Q25;
            Q25=makeQuery(id+"F3.imprint","IMPRINT",FACE,{"disambiguationData":[TD([[makeQuery(id+"F3.imprint","IMPRINT",EDGE,{"derivedFrom":sQuery(id+"F3.wireOp",EDGE,"E15.27.5")}),1.0]])]});
            var Q26;
            Q26=makeQuery(id+"F3.imprint","IMPRINT",FACE,{"disambiguationData":[TD([[makeQuery(id+"F3.imprint","IMPRINT",EDGE,{"derivedFrom":sQuery(id+"F3.wireOp",EDGE,"E15.26.5")}),1.0]])]});
            var Q27;
            Q27=makeQuery(id+"F3.imprint","IMPRINT",FACE,{"disambiguationData":[TD([[makeQuery(id+"F3.imprint","IMPRINT",EDGE,{"derivedFrom":sQuery(id+"F3.wireOp",EDGE,"E15.25.5")}),1.0]])]});
            var Q28;
            Q28=makeQuery(id+"F3.imprint","IMPRINT",FACE,{"disambiguationData":[TD([[makeQuery(id+"F3.imprint","IMPRINT",EDGE,{"derivedFrom":sQuery(id+"F3.wireOp",EDGE,"E15.24.5")}),1.0]])]});
            var Q29;
            Q29=makeQuery(id+"F3.imprint","IMPRINT",FACE,{"disambiguationData":[TD([[makeQuery(id+"F3.imprint","IMPRINT",EDGE,{"derivedFrom":sQuery(id+"F3.wireOp",EDGE,"E15.23.5")}),1.0]])]});
            var Q30;
            Q30=makeQuery(id+"F3.imprint","IMPRINT",FACE,{"disambiguationData":[TD([[makeQuery(id+"F3.imprint","IMPRINT",EDGE,{"derivedFrom":sQuery(id+"F3.wireOp",EDGE,"E15.22.5")}),1.0]])]});
            var Q31;
            Q31=makeQuery(id+"F3.imprint","IMPRINT",FACE,{"disambiguationData":[TD([[makeQuery(id+"F3.imprint","IMPRINT",EDGE,{"derivedFrom":sQuery(id+"F3.wireOp",EDGE,"E15.21.5")}),1.0]])]});
            var Q32;
            Q32=makeQuery(id+"F3.imprint","IMPRINT",FACE,{"disambiguationData":[TD([[makeQuery(id+"F3.imprint","IMPRINT",EDGE,{"derivedFrom":sQuery(id+"F3.wireOp",EDGE,"E15.20.5")}),1.0]])]});
            var Q33;
            Q33=makeQuery(id+"F3.imprint","IMPRINT",FACE,{"disambiguationData":[TD([[makeQuery(id+"F3.imprint","IMPRINT",EDGE,{"derivedFrom":sQuery(id+"F3.wireOp",EDGE,"E15.19.5")}),1.0]])]});
            var Q34;
            Q34=makeQuery(id+"F3.imprint","IMPRINT",FACE,{"disambiguationData":[TD([[makeQuery(id+"F3.imprint","IMPRINT",EDGE,{"derivedFrom":sQuery(id+"F3.wireOp",EDGE,"E15.18.5")}),1.0]])]});
            var Q35;
            Q35=makeQuery(id+"F3.imprint","IMPRINT",FACE,{"disambiguationData":[TD([[makeQuery(id+"F3.imprint","IMPRINT",EDGE,{"derivedFrom":sQuery(id+"F3.wireOp",EDGE,"E15.17.5")}),1.0]])]});
            var Q36;
            Q36=makeQuery(id+"F3.imprint","IMPRINT",FACE,{"disambiguationData":[TD([[makeQuery(id+"F3.imprint","IMPRINT",EDGE,{"derivedFrom":sQuery(id+"F3.wireOp",EDGE,"E15.16.5")}),1.0]])]});
            var Q37;
            Q37=makeQuery(id+"F3.imprint","IMPRINT",FACE,{"disambiguationData":[TD([[makeQuery(id+"F3.imprint","IMPRINT",EDGE,{"derivedFrom":sQuery(id+"F3.wireOp",EDGE,"E15.15.5")}),1.0]])]});
            var Q38;
            Q38=makeQuery(id+"F3.imprint","IMPRINT",FACE,{"disambiguationData":[TD([[makeQuery(id+"F3.imprint","IMPRINT",EDGE,{"derivedFrom":sQuery(id+"F3.wireOp",EDGE,"E15.14.5")}),1.0]])]});
            var Q39;
            Q39=makeQuery(id+"F3.imprint","IMPRINT",FACE,{"disambiguationData":[TD([[makeQuery(id+"F3.imprint","IMPRINT",EDGE,{"derivedFrom":sQuery(id+"F3.wireOp",EDGE,"E15.13.5")}),1.0]])]});
            var Q40;
            Q40=makeQuery(id+"F3.imprint","IMPRINT",FACE,{"disambiguationData":[TD([[makeQuery(id+"F3.imprint","IMPRINT",EDGE,{"derivedFrom":sQuery(id+"F3.wireOp",EDGE,"E15.12.5")}),1.0]])]});
            var Q41;
            Q41=makeQuery(id+"F3.imprint","IMPRINT",FACE,{"disambiguationData":[TD([[makeQuery(id+"F3.imprint","IMPRINT",EDGE,{"derivedFrom":sQuery(id+"F3.wireOp",EDGE,"E15.11.5")}),1.0]])]});
            var Q42;
            Q42=makeQuery(id+"F3.imprint","IMPRINT",FACE,{"disambiguationData":[TD([[makeQuery(id+"F3.imprint","IMPRINT",EDGE,{"derivedFrom":sQuery(id+"F3.wireOp",EDGE,"E15.10.5")}),1.0]])]});
            var Q43;
            Q43=makeQuery(id+"F3.imprint","IMPRINT",FACE,{"disambiguationData":[TD([[makeQuery(id+"F3.imprint","IMPRINT",EDGE,{"derivedFrom":sQuery(id+"F3.wireOp",EDGE,"E15.9.5")}),1.0]])]});
            var Q44;
            Q44=makeQuery(id+"F3.imprint","IMPRINT",FACE,{"disambiguationData":[TD([[makeQuery(id+"F3.imprint","IMPRINT",EDGE,{"derivedFrom":sQuery(id+"F3.wireOp",EDGE,"E15.8.5")}),1.0]])]});
            var Q45;
            Q45=makeQuery(id+"F3.imprint","IMPRINT",FACE,{"disambiguationData":[TD([[makeQuery(id+"F3.imprint","IMPRINT",EDGE,{"derivedFrom":sQuery(id+"F3.wireOp",EDGE,"E15.7.5")}),1.0]])]});
            var Q46;
            Q46=makeQuery(id+"F3.imprint","IMPRINT",FACE,{"disambiguationData":[TD([[makeQuery(id+"F3.imprint","IMPRINT",EDGE,{"derivedFrom":sQuery(id+"F3.wireOp",EDGE,"E15.6.5")}),1.0]])]});
            var Q47;
            Q47=makeQuery(id+"F3.imprint","IMPRINT",FACE,{"disambiguationData":[TD([[makeQuery(id+"F3.imprint","IMPRINT",EDGE,{"derivedFrom":sQuery(id+"F3.wireOp",EDGE,"E15.5.5")}),1.0]])]});
            var Q48;
            Q48=makeQuery(id+"F3.imprint","IMPRINT",FACE,{"disambiguationData":[TD([[makeQuery(id+"F3.imprint","IMPRINT",EDGE,{"derivedFrom":sQuery(id+"F3.wireOp",EDGE,"E15.4.5")}),1.0]])]});
            var Q49;
            Q49=makeQuery(id+"F3.imprint","IMPRINT",FACE,{"disambiguationData":[TD([[makeQuery(id+"F3.imprint","IMPRINT",EDGE,{"derivedFrom":sQuery(id+"F3.wireOp",EDGE,"E15.3.5")}),1.0]])]});
            var Q50;
            Q50=makeQuery(id+"F3.imprint","IMPRINT",FACE,{"disambiguationData":[TD([[makeQuery(id+"F3.imprint","IMPRINT",EDGE,{"derivedFrom":sQuery(id+"F3.wireOp",EDGE,"E15.2.5")}),1.0]])]});
            var Q51;
            Q51=makeQuery(id+"F3.imprint","IMPRINT",FACE,{"disambiguationData":[TD([[makeQuery(id+"F3.imprint","IMPRINT",EDGE,{"derivedFrom":sQuery(id+"F3.wireOp",EDGE,"E15.1.5")}),1.0]])]});
            extrude(context, id + "F4", {"entities" : qUnion([Q0, Q1, Q2, Q3, Q4, Q5, Q6, Q7, Q8, Q9, Q10, Q11, Q12, Q13, Q14, Q15, Q16, Q17, Q18, Q19, Q20, Q21, Q22, Q23, Q24, Q25, Q26, Q27, Q28, Q29, Q30, Q31, Q32, Q33, Q34, Q35, Q36, Q37, Q38, Q39, Q40, Q41, Q42, Q43, Q44, Q45, Q46, Q47, Q48, Q49, Q50, Q51]), "operationType" : NewBodyOperationType.REMOVE, "depth" : 50.8 * mm, "offsetDistance" : 25.4 * mm});
        }
    });
